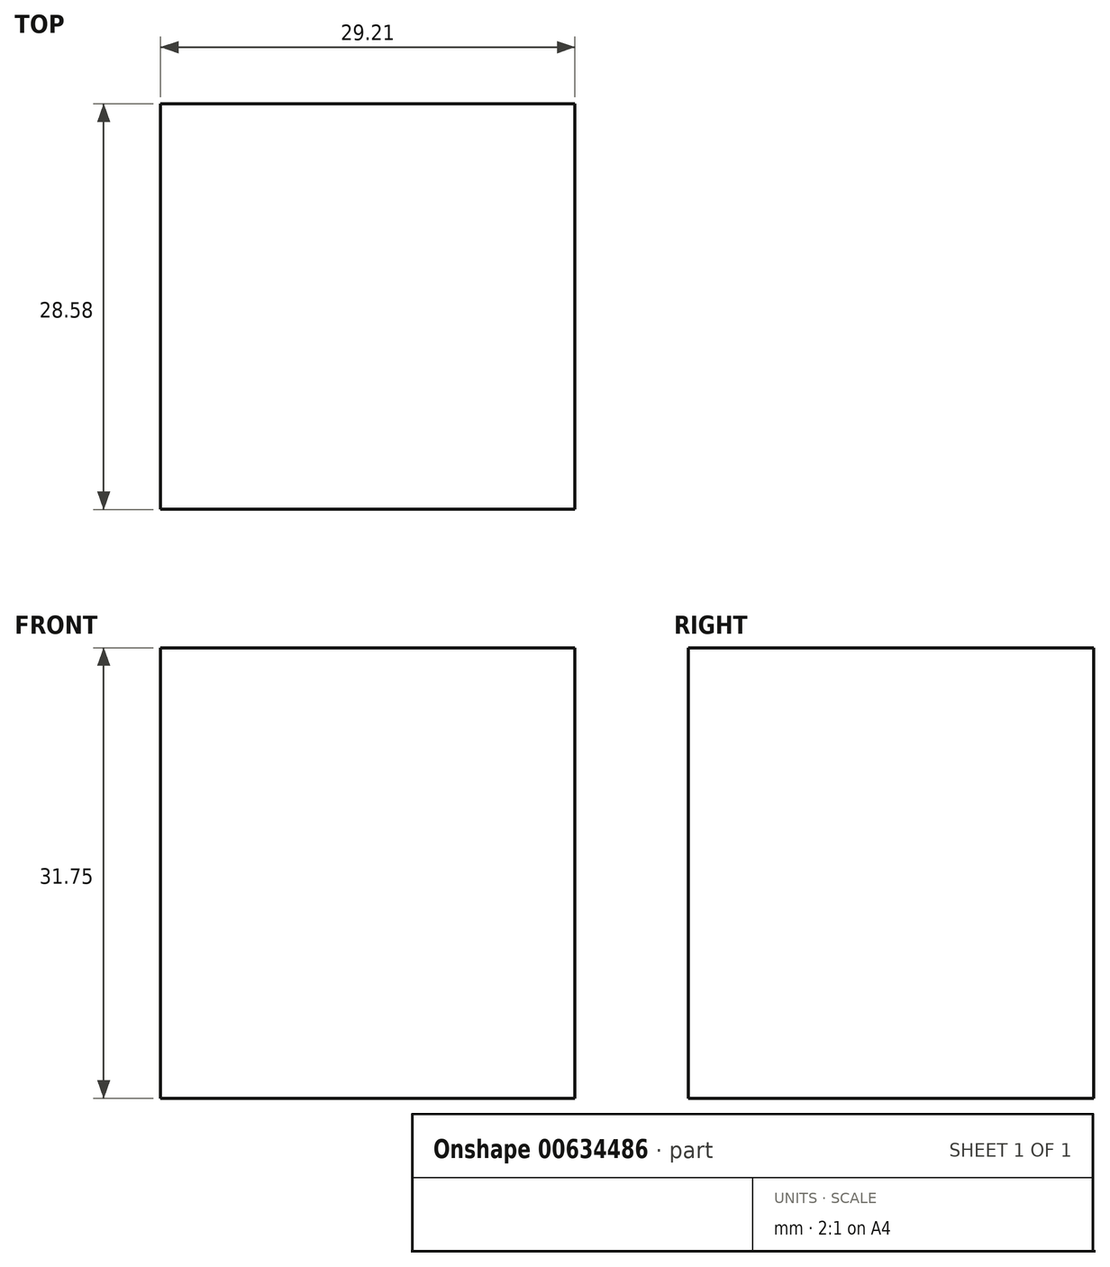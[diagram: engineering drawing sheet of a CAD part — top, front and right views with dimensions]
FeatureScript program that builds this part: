
annotation { "Feature Type Name" : "Feature", "Feature Type Description" : "" }
export const myFeature = defineFeature(function(context is Context, id is Id, definition is map)
    precondition{}
    {
        {
            var Q0;
            Q0=qCreatedBy(makeId("Top.planeOp"),FACE);
            var sketch = newSketch(context, id + "F0", { "sketchPlane" : qUnion([Q0])});
            skLineSegment(sketch, "E0.bottom", {"start": v(0, 34.43) * mm, "end": v(29.21, 34.43) * mm});
            skLineSegment(sketch, "E0.top", {"start": v(0, 5.85) * mm, "end": v(29.21, 5.85) * mm});
            skLineSegment(sketch, "E0.left", {"start": v(0, 34.43) * mm, "end": v(0, 5.85) * mm});
            skLineSegment(sketch, "E0.right", {"start": v(29.21, 34.43) * mm, "end": v(29.21, 5.85) * mm});
            skSolve(sketch);
        }
        {
            var Q0;
            Q0 = qSketchRegion(id + "F0", true);
            extrude(context, id + "F1", {"entities" : qUnion([Q0]), "depth" : 31.75 * mm, "offsetDistance" : 25.4 * mm});
        }
    });
